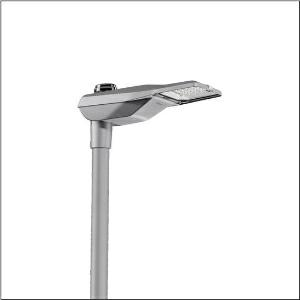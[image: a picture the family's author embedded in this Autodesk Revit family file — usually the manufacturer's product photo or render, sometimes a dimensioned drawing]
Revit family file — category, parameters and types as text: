
# Revit family: streetlight_sl_21_micro___st1_0a_5xe5d47n08db_8e26
name_source: partatom
category: Lighting Fixtures
units: mm (PartAtom-declared; Revit-internal decimal feet)

## family parameters
Cut with Voids When Loaded = No
Host = Face
Light Source = No
Part Type = Normal
Room Calculation Point = No
Round Connector Dimension = Use Diameter
Shared = No

## types (1)
- --- (1 x LED, 5320 lm, 39.1 W, 4000K)
    Apparent Load = 39 VA
    CIE Flux Codes = 37 72 97 100 100
    Color Rendering = 70
    Color Temperature = 4000K
    Default Elevation = 1800 mm
    Description = Streetlight SL 21 micro, mast luminaire, primary light control with lens, of PMMA, primary optical cover: cover, of toughened safety glass, transparent, light distribution: ST1.0a, light emission: direct distribution, primary light characteristic: asymmetric, installation type: post-top, LED, 3G 1.5mm², High Power LED, rated luminous flux: 5.320lm, luminous efficacy: 136lm/W, light colour: 740, colour temperature: 4000K, control: overheat protection, pre-setting: linear dimming characteristic, constant luminous flux control, time-dependent luminous flux control, flexible luminous flux parameterisation, mains connection: 230..240V, AC, 50/60Hz, connection cable pre-assembled, cable length: 6,5m, wiring characteristics: H07RN-F, start of lifetime: 39W, end of service life: 41W, reduction: 18W, luminaire housing, of diecast aluminium (EN AC-44300), powder-coated, Siteco® metallic grey (DB 702S), corrosivity category C5 mid according to DIN EN ISO 12944, multi-level sealing system, sealing non-destructively replaceable, inclination adjustable: 0°, 5°, 10°, 15°, length: 528mm, width: 235mm, height: 110mm, spigot size: 76/60mm (post-top), protection rating (complete): IP66, insulation class (complete): insulation class I (protective earthing), certification: CE, ENEC, ENEC+, VDE, impact resistance: IK09, permissible operating ambient temperature for outdoor applications: -40..+50°C, standard-compliant lighting for roads and squares, packaging unit: 1 piece

Light Distribution: ST1.0a
    Height = 110 mm
    Lamp = 1 x LED
    Lamp Light Flux = 5320 lm
    Lamp Power = 39.1 W
    Lamp count = 1
    Length = 528 mm
    Luminous efficacy = 136 lm/W
    Manufacturer = Siteco
    ModVariant = No
    Model = 5XE5D47N08DB
    Number of Poles = 1
    OnlyDefault = Yes
    Power Factor = 1
    Product Name = Streetlight SL 21 micro | ST1.0a
    Product group = mast luminaire | pylon top
    ProductGroupID = 6100
    Protection Class = Protection class I
    Protection Degree = IP 66
    RLX_Detail_Level = 1
    RLX_Emergency_Light_Flux = 0 lm
    RLX_Emergency_Type = 0
    RLX_Emergency_Type_DB = No
    RlxData = <blob elided: 99017 chars, md5=a9110ad8>
    Socket = socket
    Standby Power = 0 W
    System Light Flux = 5320 lm
    System Power = 39 W
    Type Comments = factory setting: luminous flux: 100 % | dim-lin: 254 | 765 mA
    Type Image = l_1294375.jpg
    URL = http://relux.com
    VarID = @adj_106279
    Voltage = 0 V
    Weight = 0.00 kg
    Width = 235 mm

## geometry (parser evidence)
native form markers: Blend x4, Sweep x11
no freeform markers — native parametric forms only
